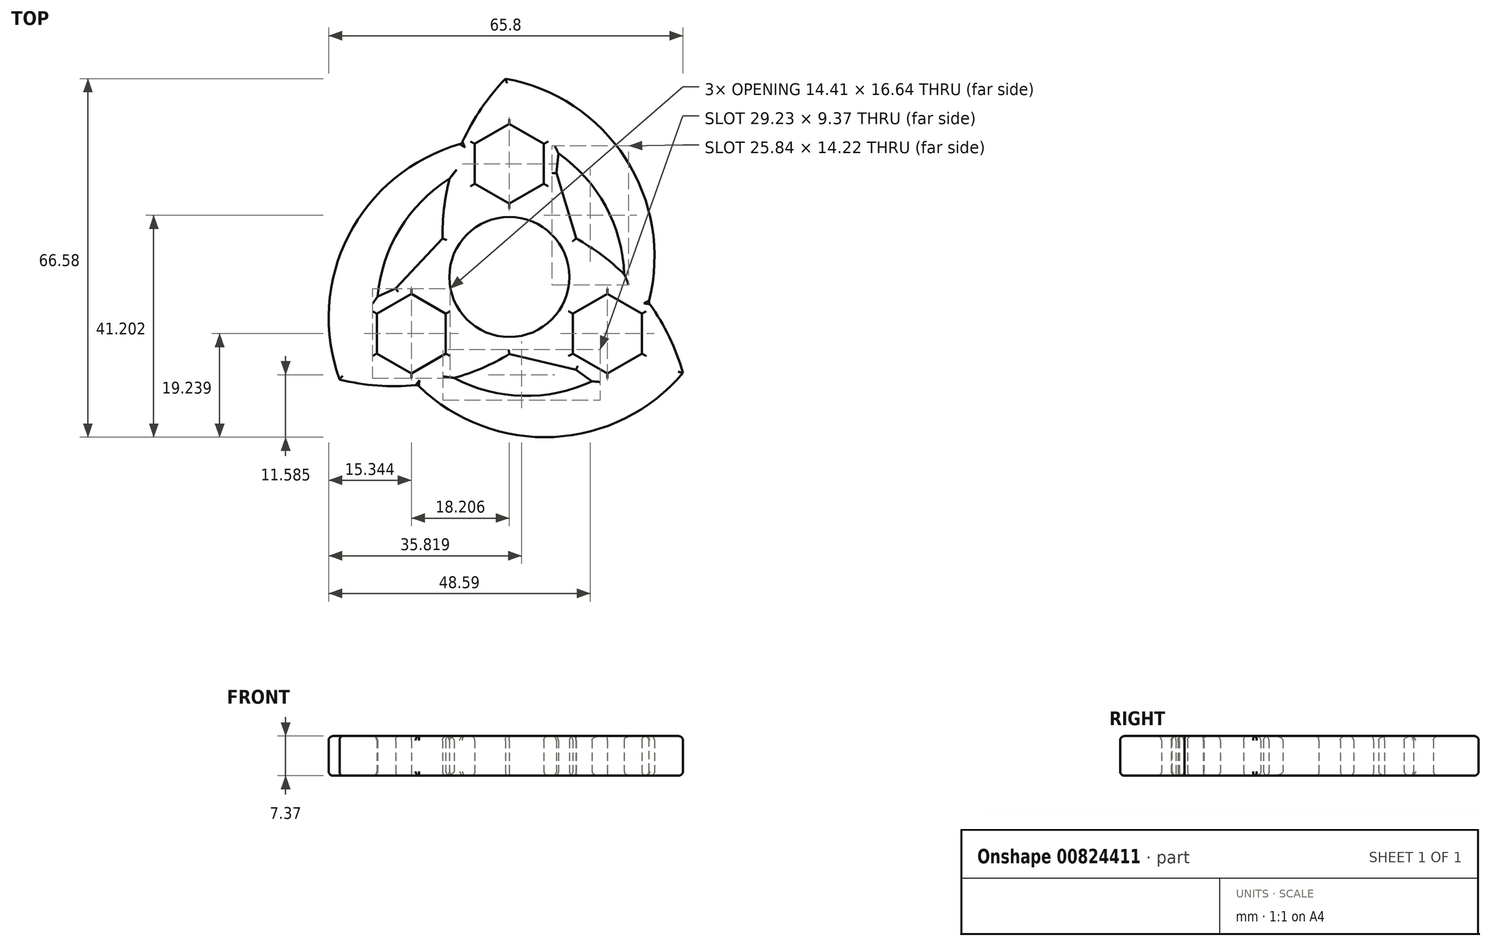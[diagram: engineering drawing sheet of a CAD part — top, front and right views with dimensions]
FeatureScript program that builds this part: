
annotation { "Feature Type Name" : "Feature", "Feature Type Description" : "" }
export const myFeature = defineFeature(function(context is Context, id is Id, definition is map)
    precondition{}
    {
        {
            var Q0;
            Q0=qCreatedBy(makeId("Top.planeOp"),FACE);
            var sketch = newSketch(context, id + "F0", { "sketchPlane" : qUnion([Q0])});
            skCircle(sketch, "E0", {"center": v(0, 0) * mm, "radius": 11.15 * mm});
            skLineSegment(sketch, "E1", {"start": v(-9.66, 5.58) * mm, "end": v(0, 0) * mm, "construction": true});
            skLineSegment(sketch, "E2", {"start": v(0, 0) * mm, "end": v(33, 19.05) * mm, "construction": true});
            skLineSegment(sketch, "E3", {"start": v(0, 0) * mm, "end": v(0, -38.1) * mm, "construction": true});
            skArc(sketch, "E4", {"start": v(-0.71, 36.83) * mm, "mid": v(-9.5, 23.16) * mm, "end": v(-12.4, 7.16) * mm});
            skArc(sketch, "E5", {"start": v(25.42, -6.29) * mm, "mid": v(22.11, 21.19) * mm, "end": v(-0.71, 36.83) * mm});
            skArc(sketch, "E6", {"start": v(21.35, 0.49) * mm, "mid": v(17.87, 13.18) * mm, "end": v(9.1, 22.98) * mm});
            skLineSegment(sketch, "E7", {"start": v(9.1, 22.98) * mm, "end": v(8.73, 19.33) * mm});
            skLineSegment(sketch, "E8", {"start": v(8.73, 19.33) * mm, "end": v(12.4, 7.16) * mm});
            skLineSegment(sketch, "E9", {"start": v(-9.66, 5.57) * mm, "end": v(-42.65, 24.63) * mm, "construction": true});
            skArc(sketch, "E10.1.0", {"start": v(-31.54, -19.03) * mm, "mid": v(-15.3, -19.81) * mm, "end": v(0, -14.32) * mm});
            skLineSegment(sketch, "E10.1.1", {"start": v(-21.11, -2.1) * mm, "end": v(-12.4, 7.16) * mm});
            skLineSegment(sketch, "E10.1.2", {"start": v(-24.45, -3.61) * mm, "end": v(-21.11, -2.1) * mm});
            skArc(sketch, "E10.1.3", {"start": v(-11.1, 18.25) * mm, "mid": v(-20.35, 8.9) * mm, "end": v(-24.45, -3.61) * mm});
            skArc(sketch, "E10.1.4", {"start": v(-7.26, 25.15) * mm, "mid": v(-29.4, 8.56) * mm, "end": v(-31.54, -19.03) * mm});
            skArc(sketch, "E10.2.0", {"start": v(32.25, -17.8) * mm, "mid": v(24.8, -3.34) * mm, "end": v(12.4, 7.16) * mm});
            skLineSegment(sketch, "E10.2.1", {"start": v(12.38, -17.23) * mm, "end": v(0, -14.33) * mm});
            skLineSegment(sketch, "E10.2.2", {"start": v(15.35, -19.37) * mm, "end": v(12.38, -17.23) * mm});
            skArc(sketch, "E10.2.3", {"start": v(-10.25, -18.74) * mm, "mid": v(2.48, -22.07) * mm, "end": v(15.35, -19.37) * mm});
            skArc(sketch, "E10.2.4", {"start": v(-18.15, -18.87) * mm, "mid": v(7.3, -29.74) * mm, "end": v(32.25, -17.8) * mm});
            skCircle(sketch, "E11.cCircle", {"center": v(0, 21.02) * mm, "radius": 7.4 * mm, "construction": true});
            skLineSegment(sketch, "E11.0", {"start": v(0, 28.43) * mm, "end": v(6.41, 24.73) * mm});
            skLineSegment(sketch, "E11.1", {"start": v(6.41, 24.73) * mm, "end": v(6.41, 17.32) * mm});
            skLineSegment(sketch, "E11.2", {"start": v(6.41, 17.32) * mm, "end": v(0, 13.62) * mm});
            skLineSegment(sketch, "E11.3", {"start": v(0, 13.62) * mm, "end": v(-6.41, 17.32) * mm});
            skLineSegment(sketch, "E11.4", {"start": v(-6.41, 17.32) * mm, "end": v(-6.41, 24.73) * mm});
            skLineSegment(sketch, "E11.5", {"start": v(-6.41, 24.73) * mm, "end": v(0, 28.43) * mm});
            skLineSegment(sketch, "E12.1.0", {"start": v(-18.2, -17.92) * mm, "end": v(-24.62, -14.21) * mm});
            skLineSegment(sketch, "E12.1.1", {"start": v(-24.62, -14.21) * mm, "end": v(-24.62, -6.8) * mm});
            skLineSegment(sketch, "E12.1.2", {"start": v(-24.62, -6.8) * mm, "end": v(-18.2, -3.1) * mm});
            skLineSegment(sketch, "E12.1.3", {"start": v(-18.2, -3.1) * mm, "end": v(-11.8, -6.8) * mm});
            skLineSegment(sketch, "E12.1.4", {"start": v(-11.8, -6.8) * mm, "end": v(-11.8, -14.21) * mm});
            skLineSegment(sketch, "E12.1.5", {"start": v(-11.8, -14.21) * mm, "end": v(-18.2, -17.92) * mm});
            skLineSegment(sketch, "E12.2.0", {"start": v(24.62, -6.8) * mm, "end": v(24.62, -14.21) * mm});
            skLineSegment(sketch, "E12.2.1", {"start": v(24.62, -14.21) * mm, "end": v(18.2, -17.92) * mm});
            skLineSegment(sketch, "E12.2.2", {"start": v(18.2, -17.92) * mm, "end": v(11.8, -14.21) * mm});
            skLineSegment(sketch, "E12.2.3", {"start": v(11.8, -14.21) * mm, "end": v(11.8, -6.8) * mm});
            skLineSegment(sketch, "E12.2.4", {"start": v(11.8, -6.8) * mm, "end": v(18.2, -3.1) * mm});
            skLineSegment(sketch, "E12.2.5", {"start": v(18.2, -3.1) * mm, "end": v(24.62, -6.8) * mm});
            skSolve(sketch);
        }
        {
            var Q0;
            Q0=qSketchRegion(id+"F0",true);
            extrude(context, id + "F1", {"entities" : qUnion([Q0]), "depth" : 7.37 * mm, "offsetDistance" : 25.4 * mm});
        }
        {
            var Q0;
            Q0=makeQuery(id+"F1.opExtrude","CAP_FACE",FACE,{"disambiguationData":[OSD([sQuery(id+"F0.wireOp",EDGE,"E0"),sQuery(id+"F0.wireOp",EDGE,"E4"),sQuery(id+"F0.wireOp",EDGE,"E5"),sQuery(id+"F0.wireOp",EDGE,"E6"),sQuery(id+"F0.wireOp",EDGE,"E7"),sQuery(id+"F0.wireOp",EDGE,"E8"),sQuery(id+"F0.wireOp",EDGE,"E10.1.0"),sQuery(id+"F0.wireOp",EDGE,"E10.1.1"),sQuery(id+"F0.wireOp",EDGE,"E10.1.2"),sQuery(id+"F0.wireOp",EDGE,"E10.1.3"),sQuery(id+"F0.wireOp",EDGE,"E10.1.4"),sQuery(id+"F0.wireOp",EDGE,"E10.2.0"),sQuery(id+"F0.wireOp",EDGE,"E10.2.1"),sQuery(id+"F0.wireOp",EDGE,"E10.2.2"),sQuery(id+"F0.wireOp",EDGE,"E10.2.3"),sQuery(id+"F0.wireOp",EDGE,"E10.2.4"),sQuery(id+"F0.wireOp",EDGE,"E11.0"),sQuery(id+"F0.wireOp",EDGE,"E11.1"),sQuery(id+"F0.wireOp",EDGE,"E11.2"),sQuery(id+"F0.wireOp",EDGE,"E11.3"),sQuery(id+"F0.wireOp",EDGE,"E11.4"),sQuery(id+"F0.wireOp",EDGE,"E11.5"),sQuery(id+"F0.wireOp",EDGE,"E12.1.0"),sQuery(id+"F0.wireOp",EDGE,"E12.1.1"),sQuery(id+"F0.wireOp",EDGE,"E12.1.2"),sQuery(id+"F0.wireOp",EDGE,"E12.1.3"),sQuery(id+"F0.wireOp",EDGE,"E12.1.4"),sQuery(id+"F0.wireOp",EDGE,"E12.1.5"),sQuery(id+"F0.wireOp",EDGE,"E12.2.0"),sQuery(id+"F0.wireOp",EDGE,"E12.2.1"),sQuery(id+"F0.wireOp",EDGE,"E12.2.2"),sQuery(id+"F0.wireOp",EDGE,"E12.2.3"),sQuery(id+"F0.wireOp",EDGE,"E12.2.4"),sQuery(id+"F0.wireOp",EDGE,"E12.2.5")])],"isStart":false});
            var Q1;
            Q1=makeQuery(id+"F1.opExtrude","CAP_FACE",FACE,{"disambiguationData":[OSD([sQuery(id+"F0.wireOp",EDGE,"E0"),sQuery(id+"F0.wireOp",EDGE,"E4"),sQuery(id+"F0.wireOp",EDGE,"E5"),sQuery(id+"F0.wireOp",EDGE,"E6"),sQuery(id+"F0.wireOp",EDGE,"E7"),sQuery(id+"F0.wireOp",EDGE,"E8"),sQuery(id+"F0.wireOp",EDGE,"E10.1.0"),sQuery(id+"F0.wireOp",EDGE,"E10.1.1"),sQuery(id+"F0.wireOp",EDGE,"E10.1.2"),sQuery(id+"F0.wireOp",EDGE,"E10.1.3"),sQuery(id+"F0.wireOp",EDGE,"E10.1.4"),sQuery(id+"F0.wireOp",EDGE,"E10.2.0"),sQuery(id+"F0.wireOp",EDGE,"E10.2.1"),sQuery(id+"F0.wireOp",EDGE,"E10.2.2"),sQuery(id+"F0.wireOp",EDGE,"E10.2.3"),sQuery(id+"F0.wireOp",EDGE,"E10.2.4"),sQuery(id+"F0.wireOp",EDGE,"E11.0"),sQuery(id+"F0.wireOp",EDGE,"E11.1"),sQuery(id+"F0.wireOp",EDGE,"E11.2"),sQuery(id+"F0.wireOp",EDGE,"E11.3"),sQuery(id+"F0.wireOp",EDGE,"E11.4"),sQuery(id+"F0.wireOp",EDGE,"E11.5"),sQuery(id+"F0.wireOp",EDGE,"E12.1.0"),sQuery(id+"F0.wireOp",EDGE,"E12.1.1"),sQuery(id+"F0.wireOp",EDGE,"E12.1.2"),sQuery(id+"F0.wireOp",EDGE,"E12.1.3"),sQuery(id+"F0.wireOp",EDGE,"E12.1.4"),sQuery(id+"F0.wireOp",EDGE,"E12.1.5"),sQuery(id+"F0.wireOp",EDGE,"E12.2.0"),sQuery(id+"F0.wireOp",EDGE,"E12.2.1"),sQuery(id+"F0.wireOp",EDGE,"E12.2.2"),sQuery(id+"F0.wireOp",EDGE,"E12.2.3"),sQuery(id+"F0.wireOp",EDGE,"E12.2.4"),sQuery(id+"F0.wireOp",EDGE,"E12.2.5")])],"isStart":true});
            fillet(context, id + "F2", {"entities" : qUnion([Q0, Q1]), "radius" : 0.8 * mm, "tangentPropagation" : true, "allowEdgeOverflow" : false});
        }
        {
            var Q0;
            Q0=makeQuery(id+"F1.opExtrude","SWEPT_EDGE",EDGE,{"disambiguationData":[OSD([sQuery(id+"F0.wireOp",EDGE,"E10.1.0"),sQuery(id+"F0.wireOp",EDGE,"E10.2.4")])]});
            var Q1;
            Q1=makeQuery(id+"F1.opExtrude","SWEPT_EDGE",EDGE,{"disambiguationData":[OSD([sQuery(id+"F0.wireOp",EDGE,"E4"),sQuery(id+"F0.wireOp",EDGE,"E10.1.4")])]});
            var Q2;
            Q2=makeQuery(id+"F1.opExtrude","SWEPT_EDGE",EDGE,{"disambiguationData":[OSD([sQuery(id+"F0.wireOp",EDGE,"E5"),sQuery(id+"F0.wireOp",EDGE,"E10.2.0")])]});
            fillet(context, id + "F3", {"entities" : qUnion([Q0, Q1, Q2]), "radius" : 0.8 * mm, "tangentPropagation" : true, "allowEdgeOverflow" : false});
        }
    });
